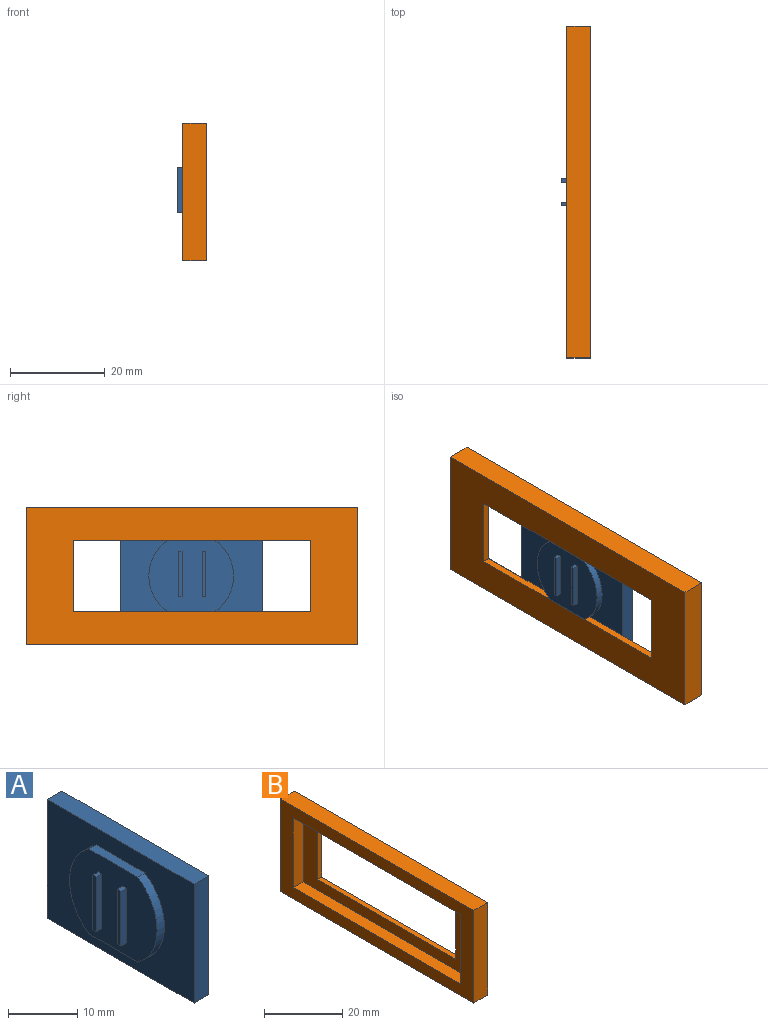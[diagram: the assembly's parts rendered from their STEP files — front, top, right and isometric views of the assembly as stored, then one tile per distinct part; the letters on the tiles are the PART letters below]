
ASSEMBLY  parts=2 mates=1
PART A: 21 faces, bbox 5.6x30x21 mm
  f0: plane 30x21mm, normal (-1,0,0), area 396.9mm2, adj f1,f2,f3,f4,f6,f7,f8,f9
  f1: plane 30x3mm, normal (0,0,1), area 90mm2, adj f0,f2,f4,f5
  f2: plane 21x3mm, normal (0,-1,0), area 63mm2, adj f0,f1,f3,f5
  f3: plane 30x3mm, normal (0,0,-1), area 90mm2, adj f0,f2,f4,f5
  f4: plane 21x3mm, normal (0,1,0), area 63mm2, adj f0,f1,f3,f5
  f5: plane 30x21mm, normal (1,0,0), area 630mm2, adj f1,f2,f3,f4
  f6: plane 10x1.5mm, normal (0,0,-1), area 15mm2, adj f0,f7,f9,f10
  f7: cylinder r=9.1mm len=15mm, axis (1,0,0), area 26.4mm2, adj f0,f6,f8,f10
  f8: plane 10x1.5mm, normal (0,0,1), area 15mm2, adj f0,f7,f9,f10
  f9: cylinder r=9.1mm len=15mm, axis (1,0,0), area 26.4mm2, adj f0,f6,f8,f10
  f10: plane 17.89x15mm, normal (-1,0,0), area 218.7mm2, adj f6,f7,f8,f9,f11,f12,f13,f14
  f11: plane 1.1x0.75mm, normal (0,0,-1), area 0.8mm2, adj f10,f12,f14,f15
  f12: plane 9.65x1.1mm, normal (0,-1,0), area 10.6mm2, adj f10,f11,f13,f15
  f13: plane 1.1x0.75mm, normal (0,0,1), area 0.8mm2, adj f10,f12,f14,f15
  f14: plane 9.65x1.1mm, normal (0,1,0), area 10.6mm2, adj f10,f11,f13,f15
  f15: plane 9.65x0.75mm, normal (-1,0,0), area 7.2mm2, adj f11,f12,f13,f14
  f16: plane 1.1x0.75mm, normal (0,0,-1), area 0.8mm2, adj f10,f17,f19,f20
  f17: plane 9.65x1.1mm, normal (0,-1,0), area 10.6mm2, adj f10,f16,f18,f20
  f18: plane 1.1x0.75mm, normal (0,0,1), area 0.8mm2, adj f10,f17,f19,f20
  f19: plane 9.65x1.1mm, normal (0,1,0), area 10.6mm2, adj f10,f16,f18,f20
  f20: plane 9.65x0.75mm, normal (-1,0,0), area 7.2mm2, adj f16,f17,f18,f19
PART B: 15 faces, bbox 5x70x29 mm
  f0: plane 50x1.5mm, normal (0,0,-1), area 75mm2, adj f1,f7,f8,f14
  f1: plane 15x1.5mm, normal (0,-1,0), area 22.5mm2, adj f0,f2,f8,f14
  f2: plane 50x1.5mm, normal (0,0,1), area 75mm2, adj f1,f7,f8,f14
  f3: plane 29x5mm, normal (0,1,0), area 145mm2, adj f4,f6,f8,f9
  f4: plane 70x5mm, normal (0,0,1), area 350mm2, adj f3,f5,f8,f9
  f5: plane 29x5mm, normal (0,-1,0), area 145mm2, adj f4,f6,f8,f9
  f6: plane 70x5mm, normal (0,0,-1), area 350mm2, adj f3,f5,f8,f9
  f7: plane 15x1.5mm, normal (0,1,0), area 22.5mm2, adj f0,f2,f8,f14
  f8: plane 70x29mm, normal (1,0,0), area 1280mm2, adj f0,f1,f2,f3,f4,f5,f6,f7
  f9: plane 70x29mm, normal (-1,0,0), area 706.2mm2, adj f3,f4,f5,f6,f10,f11,f12,f13
  f10: plane 60.6x3.5mm, normal (0,0,1), area 212.1mm2, adj f9,f11,f13,f14
  f11: plane 21.84x3.5mm, normal (0,-1,0), area 76.5mm2, adj f9,f10,f12,f14
  f12: plane 60.6x3.5mm, normal (0,0,-1), area 212.1mm2, adj f9,f11,f13,f14
  f13: plane 21.84x3.5mm, normal (0,1,0), area 76.5mm2, adj f9,f10,f12,f14
  f14: plane 60.6x21.84mm, normal (-1,0,0), area 573.8mm2, adj f0,f1,f2,f7,f10,f11,f12,f13
PLACE A rot(axis=(1,0,0),180deg) t=(-21.5,-21.47,8.13)mm
PLACE B rot(axis=(0,0,1),180deg) t=(-18,-14.35,5.95)mm
MATE parallel A.f9 <-> B.f8  axis (-1,0,0) through (-23,-14.35,5.95)mm
